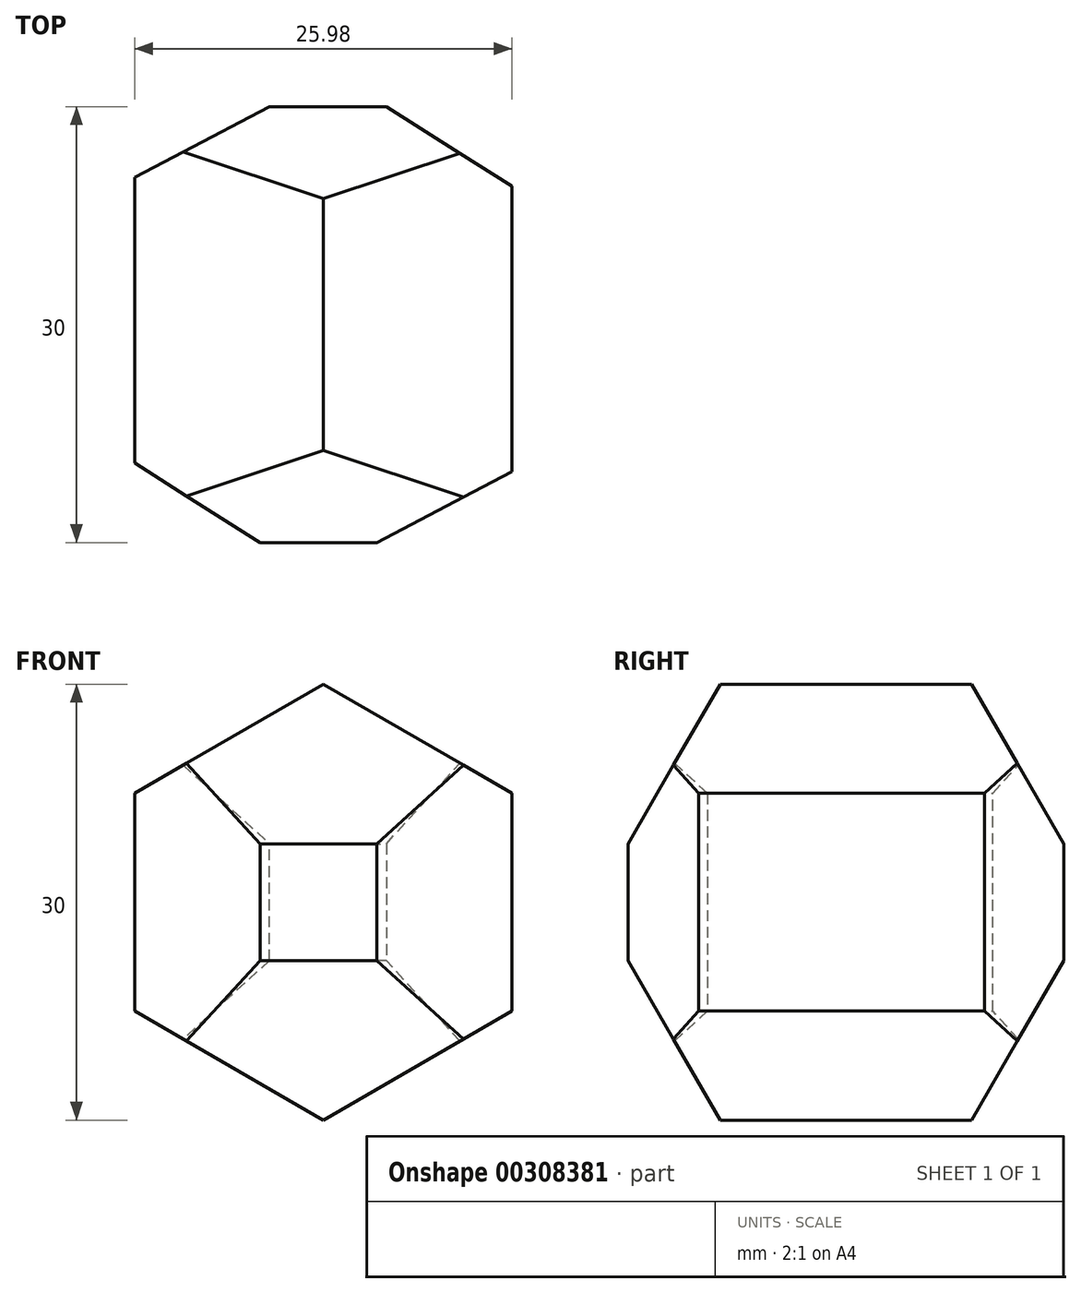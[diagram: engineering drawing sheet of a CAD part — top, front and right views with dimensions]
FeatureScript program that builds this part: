
annotation { "Feature Type Name" : "Feature", "Feature Type Description" : "" }
export const myFeature = defineFeature(function(context is Context, id is Id, definition is map)
    precondition{}
    {
        {
            var Q0;
            Q0=qCreatedBy(makeId("Top.planeOp"),FACE);
            var sketch = newSketch(context, id + "F0", { "sketchPlane" : qUnion([Q0])});
            skCircle(sketch, "E0.cCircle", {"center": v(0, 0) * mm, "radius": 15 * mm, "construction": true});
            skLineSegment(sketch, "E0.0", {"start": v(15.34, 8.05) * mm, "end": v(14.64, -9.26) * mm});
            skLineSegment(sketch, "E0.1", {"start": v(14.64, -9.26) * mm, "end": v(-0.7, -17.3) * mm});
            skLineSegment(sketch, "E0.2", {"start": v(-0.7, -17.3) * mm, "end": v(-15.34, -8.05) * mm});
            skLineSegment(sketch, "E0.3", {"start": v(-15.34, -8.05) * mm, "end": v(-14.64, 9.26) * mm});
            skLineSegment(sketch, "E0.4", {"start": v(-14.64, 9.26) * mm, "end": v(0.7, 17.3) * mm});
            skLineSegment(sketch, "E0.5", {"start": v(0.7, 17.3) * mm, "end": v(15.34, 8.05) * mm});
            skPoint(sketch, "E0.0.midPoint", {"position": v(14.99, -0.6) * mm});
            skLineSegment(sketch, "E1", {"start": v(0, 0) * mm, "end": v(-0.7, -17.3) * mm, "construction": true});
            skSolve(sketch);
        }
        {
            var Q0;
            Q0 = qSketchRegion(id + "F0", true);
            extrude(context, id + "F1", {"entities" : qUnion([Q0]), "endBound" : BoundingType.SYMMETRIC, "depth" : 30 * mm});
        }
        {
            var Q0;
            Q0=qCreatedBy(makeId("Right.planeOp"),FACE);
            var sketch = newSketch(context, id + "F2", { "sketchPlane" : qUnion([Q0])});
            skCircle(sketch, "E2.cCircle", {"center": v(0, 0) * mm, "radius": 15 * mm, "construction": true});
            skLineSegment(sketch, "E2.0", {"start": v(-8.66, 15) * mm, "end": v(8.66, 15) * mm});
            skLineSegment(sketch, "E2.1", {"start": v(8.66, 15) * mm, "end": v(17.32, 0) * mm});
            skLineSegment(sketch, "E2.2", {"start": v(17.32, 0) * mm, "end": v(8.66, -15) * mm});
            skLineSegment(sketch, "E2.3", {"start": v(8.66, -15) * mm, "end": v(-8.66, -15) * mm});
            skLineSegment(sketch, "E2.4", {"start": v(-8.66, -15) * mm, "end": v(-17.32, 0) * mm});
            skLineSegment(sketch, "E2.5", {"start": v(-17.32, 0) * mm, "end": v(-8.66, 15) * mm});
            skPoint(sketch, "E2.0.midPoint", {"position": v(0, 15) * mm});
            skSolve(sketch);
        }
        {
            var Q0;
            Q0 = qSketchRegion(id + "F2", true);
            extrude(context, id + "F3", {"entities" : qUnion([Q0]), "operationType" : NewBodyOperationType.INTERSECT, "endBound" : BoundingType.SYMMETRIC, "depth" : 30 * mm});
        }
        {
            var Q0;
            Q0=qCreatedBy(makeId("Front.planeOp"),FACE);
            var sketch = newSketch(context, id + "F4", { "sketchPlane" : qUnion([Q0])});
            skCircle(sketch, "E3.cCircle", {"center": v(0, 0) * mm, "radius": 13 * mm, "construction": true});
            skLineSegment(sketch, "E3.0", {"start": v(-13, -7.5) * mm, "end": v(-13, 7.5) * mm});
            skLineSegment(sketch, "E3.1", {"start": v(-13, 7.5) * mm, "end": v(0, 15) * mm});
            skLineSegment(sketch, "E3.2", {"start": v(0, 15) * mm, "end": v(13, 7.5) * mm});
            skLineSegment(sketch, "E3.3", {"start": v(13, 7.5) * mm, "end": v(13, -7.5) * mm});
            skLineSegment(sketch, "E3.4", {"start": v(13, -7.5) * mm, "end": v(0, -15) * mm});
            skLineSegment(sketch, "E3.5", {"start": v(0, -15) * mm, "end": v(-13, -7.5) * mm});
            skPoint(sketch, "E3.0.midPoint", {"position": v(-13, 0) * mm});
            skLineSegment(sketch, "E4", {"start": v(0, -15) * mm, "end": v(0, 0) * mm, "construction": true});
            skSolve(sketch);
        }
        {
            var Q0;
            Q0 = qSketchRegion(id + "F4", true);
            extrude(context, id + "F5", {"entities" : qUnion([Q0]), "operationType" : NewBodyOperationType.INTERSECT, "endBound" : BoundingType.SYMMETRIC, "depth" : 30 * mm});
        }
    });
